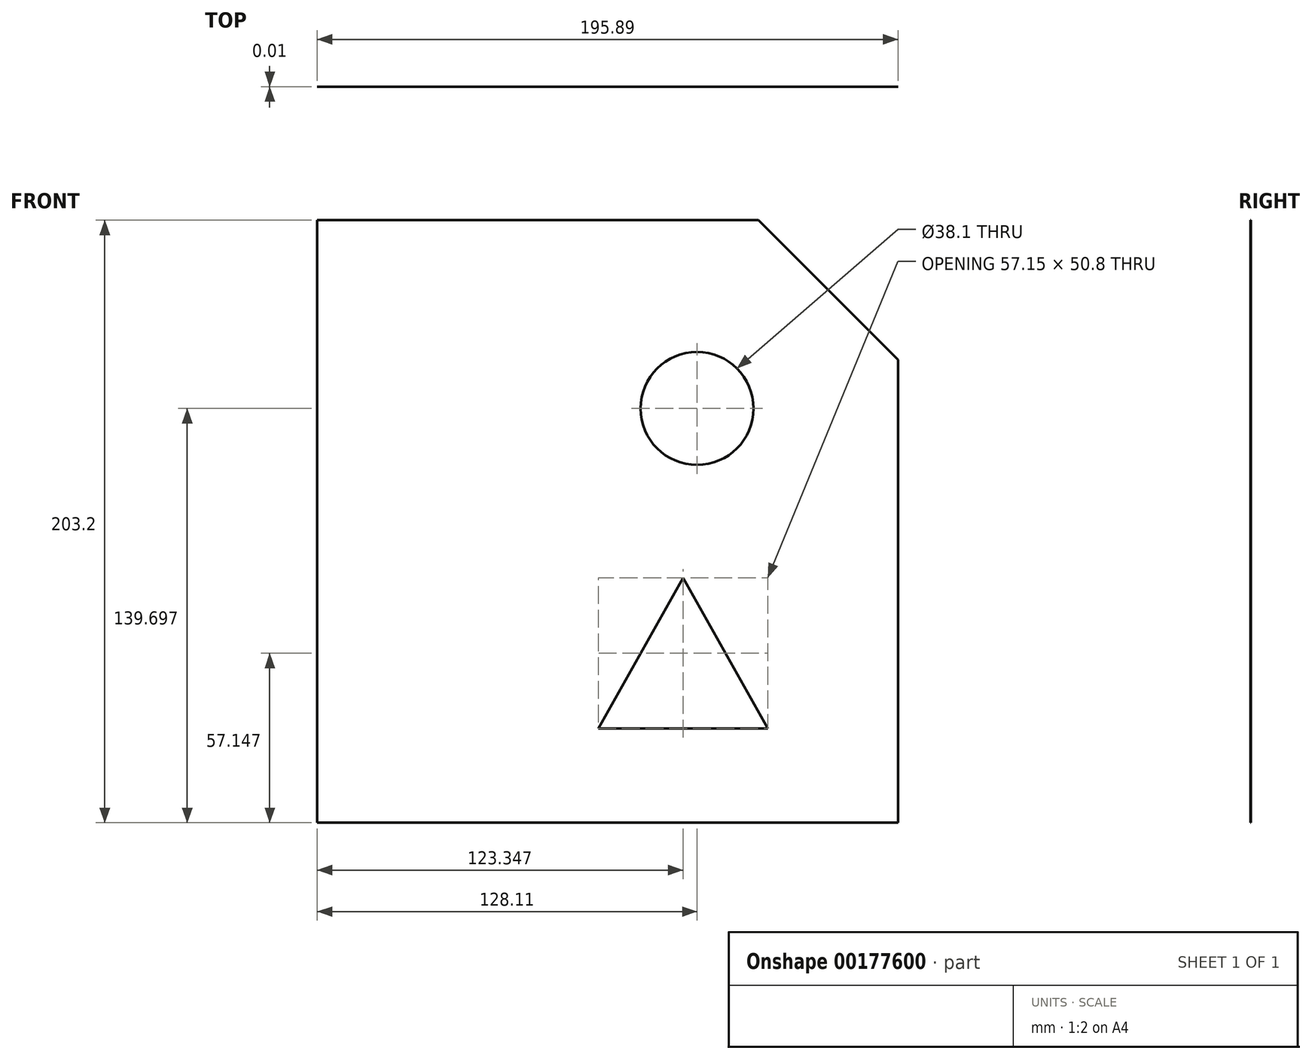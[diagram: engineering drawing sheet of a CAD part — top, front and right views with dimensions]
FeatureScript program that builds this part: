
annotation { "Feature Type Name" : "Feature", "Feature Type Description" : "" }
export const myFeature = defineFeature(function(context is Context, id is Id, definition is map)
    precondition{}
    {
        {
            var Q0;
            Q0=qCreatedBy(makeId("Front.planeOp"),FACE);
            var sketch = newSketch(context, id + "F0", { "sketchPlane" : qUnion([Q0])});
            skLineSegment(sketch, "E0.bottom", {"start": v(-84.2, 117.09) * mm, "end": v(68.2, 117.09) * mm});
            skLineSegment(sketch, "E0.top", {"start": v(-84.2, -86.11) * mm, "end": v(119, -86.11) * mm});
            skLineSegment(sketch, "E0.left", {"start": v(-84.2, 117.09) * mm, "end": v(-84.2, -86.11) * mm});
            skLineSegment(sketch, "E0.right", {"start": v(119, 66.29) * mm, "end": v(119, -86.11) * mm});
            skLineSegment(sketch, "E1", {"start": v(68.2, 117.09) * mm, "end": v(119, 66.29) * mm});
            skCircle(sketch, "E2", {"center": v(47.57, 53.59) * mm, "radius": 19.05 * mm});
            skLineSegment(sketch, "E3", {"start": v(42.8, -3.56) * mm, "end": v(14.23, -54.36) * mm});
            skLineSegment(sketch, "E4", {"start": v(14.23, -54.36) * mm, "end": v(71.38, -54.36) * mm});
            skLineSegment(sketch, "E5", {"start": v(71.38, -54.36) * mm, "end": v(42.8, -3.56) * mm});
            skSolve(sketch);
        }
        {
            var Q0;
            Q0 = qSketchRegion(id + "F0", true);
            extrude(context, id + "F1", {"entities" : qUnion([Q0]), "depth" : 3 / 203.2 * mm});
        }
        {
            var Q0;
            Q0=makeQuery(id+"F1.opExtrude","CAP_EDGE",EDGE,{"disambiguationData":[OSD([sQuery(id+"F0.wireOp",EDGE,"E0.right")])],"isStart":false});
            chamfer(context, id + "F2", {"entities" : qUnion([Q0]), "chamferType" : ChamferType.OFFSET_ANGLE, "width" : 6.35 * mm, "oppositeDirection" : false, "angle" : 30 * degree, "tangentPropagation" : true});
        }
        {
            var Q0;
            Q0=makeQuery(id+"F1.opExtrude","CAP_EDGE",EDGE,{"disambiguationData":[OSD([sQuery(id+"F0.wireOp",EDGE,"E0.left")])],"isStart":false});
            chamfer(context, id + "F3", {"entities" : qUnion([Q0]), "chamferType" : ChamferType.OFFSET_ANGLE, "width" : 6.35 * mm, "oppositeDirection" : true, "angle" : 30 * degree, "tangentPropagation" : true});
        }
    });
